# Revit family: Franke_A1000_FM_CM_FW(CN)
name_source: partatom
category: Specialty Equipment
revit_build: Autodesk Revit 2015 (Build: 20140606_1530(x64)
units: mm (PartAtom-declared; Revit-internal decimal feet)

## types (2) — shared parameters
Assembly Code = fully automatic coffee machine
Cycle (A1000) = 50 Hz
Cycle Alternative (A1000) = 0 Hz
Depth (mm) = 600 mm
Description = A1000 fully automatic coffee machine
Energy loss acc. to DIN 18873 (A1000 incl. SU12 FM) = 3.165 kWh/24 h - 400 V 16 A
Height (mm) = 796 mm  [stored 2.61155 ft]
Incoming water (cold water) = 8 mm  [stored 0.0262467 ft]
Keynote = fully automatic coffee machine
Manufacturer = Franke
Max Overcurrent Protection (A1000) = 16 A
Model = A1000 FM CM FW
Noise emission = 70 dB
Number of Nutral Conductors (A1000) = 1
Number of Poles (A1000) = 3
Number of Protective Conductors (A1000) = 1
URL = https://www.franke.com
Volts max. (A1000) = 0 V
Volts min. (A1000) = 380 V
Wastewater = 9 mm  [stored 0.0295276 ft]
Water pressure = 800000.0 Pa
Water pressure (with filter) = 600000.0 Pa
Watts max. (A1000) = 7900 W
Watts min. (A1000) = 6700 W
Weight = 58 kg
Width (mm) = 340 mm  [stored 1.11549 ft]
zero-valued in all types: Cost

## per-type parameters (varying)
| type | Frontcover |
| A1000 FM CM FW(380V/black line/CN) | Franke Black |
| A1000 FM CM FW(380V/anthracite/CN) | Franke Anthracite |

note: [stored X ft] marks values corroborated as IEEE doubles in the binary element streams (Revit-internal decimal feet)

## geometry (parser evidence)
native form markers: Extrusion x1
no freeform markers — native parametric forms only
